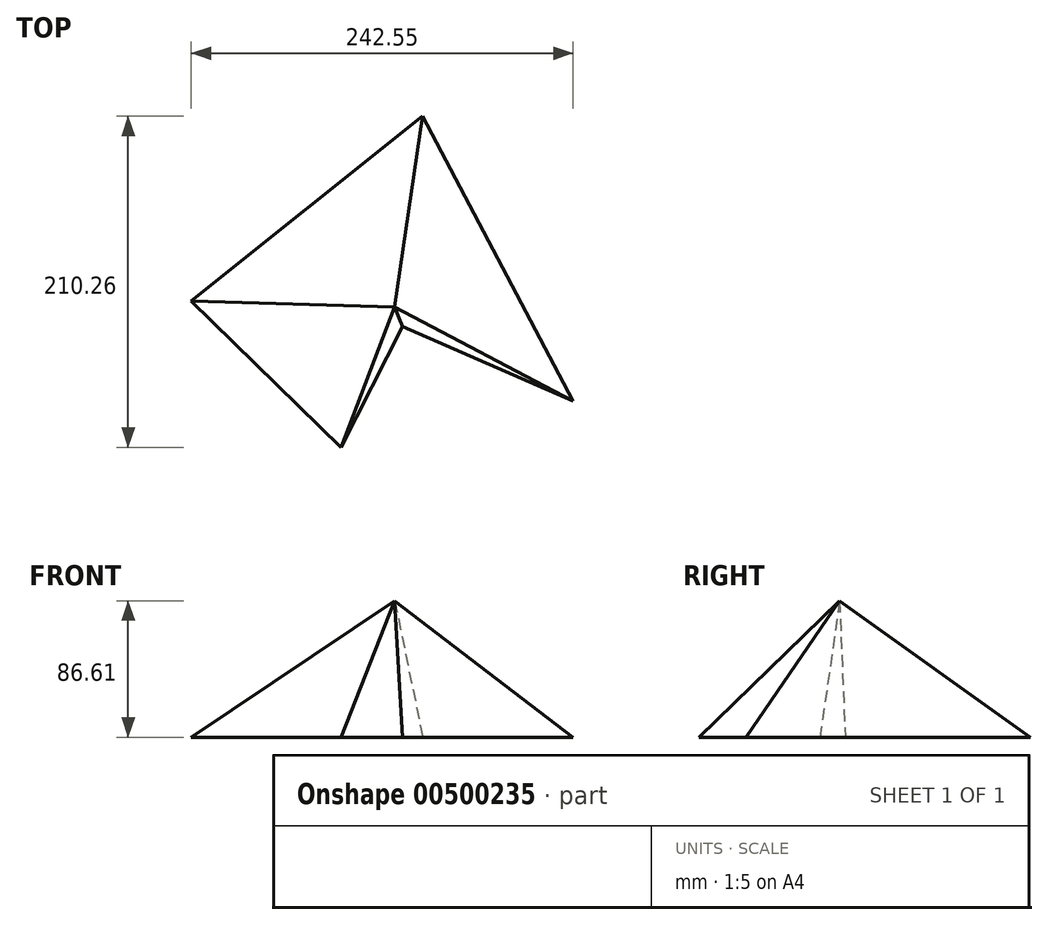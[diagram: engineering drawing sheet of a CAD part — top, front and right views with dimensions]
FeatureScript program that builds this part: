
annotation { "Feature Type Name" : "Feature", "Feature Type Description" : "" }
export const myFeature = defineFeature(function(context is Context, id is Id, definition is map)
    precondition{}
    {
        {
            var Q0;
            Q0=qCreatedBy(makeId("Top.planeOp"),FACE);
            var sketch = newSketch(context, id + "F0", { "sketchPlane" : qUnion([Q0])});
            skLineSegment(sketch, "E0", {"start": v(-129.17, 3.62) * mm, "end": v(-34.2, -89.2) * mm});
            skLineSegment(sketch, "E1", {"start": v(-34.2, -89.2) * mm, "end": v(4.96, -12.39) * mm});
            skLineSegment(sketch, "E2", {"start": v(4.96, -12.39) * mm, "end": v(113.38, -59.6) * mm});
            skLineSegment(sketch, "E3", {"start": v(113.38, -59.6) * mm, "end": v(17.84, 121.06) * mm});
            skLineSegment(sketch, "E4", {"start": v(17.84, 121.06) * mm, "end": v(-129.17, 3.62) * mm});
            skSolve(sketch);
        }
        {
            var Q0;
            Q0=qCreatedBy(makeId("Top.planeOp"),FACE);
            cPlane(context, id + "F1", {"entities" : qUnion([Q0]), "cplaneType" : CPlaneType.OFFSET, "offset" : 86.61 * mm, "width" : 152.4 * mm, "height" : 152.4 * mm});
        }
        {
            var Q0;
            Q0=qCreatedBy(id+"F1.planeOp",FACE);
            var sketch = newSketch(context, id + "F2", { "sketchPlane" : qUnion([Q0])});
            skPoint(sketch, "E5", {"position": v(0, 0) * mm});
            skSolve(sketch);
        }
        {
            var Q0;
            Q0=sQuery(id+"F2.wireOp",VERTEX,"E5");
            var Q1;
            Q1=makeQuery(id+"F0.imprint","IMPRINT",FACE,{"disambiguationData":[TD([[makeQuery(id+"F0.imprint","IMPRINT",EDGE,{"derivedFrom":sQuery(id+"F0.wireOp",EDGE,"E0")}),1.0]])]});
            loft(context, id + "F3", {"sheetProfilesArray" : [{ "sheetProfileEntities" : qUnion([Q0]) }, { "sheetProfileEntities" : qUnion([Q1]) }]});
        }
    });
